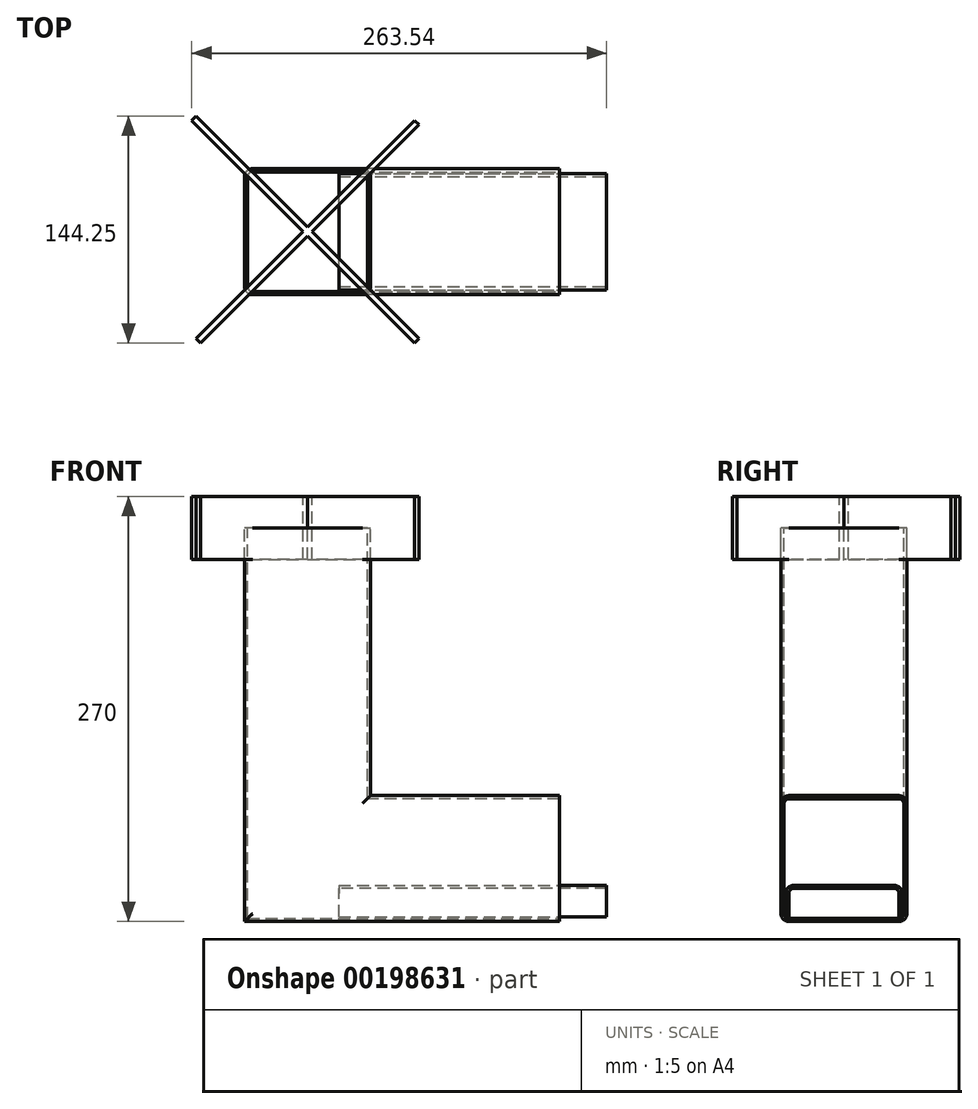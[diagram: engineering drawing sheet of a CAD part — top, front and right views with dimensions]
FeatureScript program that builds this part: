
annotation { "Feature Type Name" : "Feature", "Feature Type Description" : "" }
export const myFeature = defineFeature(function(context is Context, id is Id, definition is map)
    precondition{}
    {
        {
            var Q0;
            Q0=qCreatedBy(makeId("Front.planeOp"),FACE);
            var sketch = newSketch(context, id + "F0", { "sketchPlane" : qUnion([Q0])});
            skLineSegment(sketch, "E0.bottom", {"start": v(0, 0) * mm, "end": v(80, 0) * mm});
            skLineSegment(sketch, "E0.top", {"start": v(0, 250) * mm, "end": v(80, 250) * mm});
            skLineSegment(sketch, "E0.left", {"start": v(0, 0) * mm, "end": v(0, 250) * mm});
            skLineSegment(sketch, "E0.right", {"start": v(80, 0) * mm, "end": v(80, 250) * mm});
            skLineSegment(sketch, "E1", {"start": v(0, 0) * mm, "end": v(200, 0) * mm});
            skLineSegment(sketch, "E2", {"start": v(200, 0) * mm, "end": v(200, 80) * mm});
            skLineSegment(sketch, "E3", {"start": v(200, 80) * mm, "end": v(80, 80) * mm});
            skSolve(sketch);
        }
        {
            var Q0;
            Q0 = qSketchRegion(id + "F0", true);
            extrude(context, id + "F1", {"entities" : qUnion([Q0]), "depth" : 80 * mm});
        }
        {
            var Q0;
            Q0=makeQuery(id+"F1.opExtrude","CAP_EDGE",EDGE,{"disambiguationData":[OSD([sQuery(id+"F0.wireOp",EDGE,"E0.right")])],"isStart":false});
            var Q1;
            Q1=makeQuery(id+"F1.opExtrude","CAP_EDGE",EDGE,{"disambiguationData":[OSD([sQuery(id+"F0.wireOp",EDGE,"E0.right")])],"isStart":true});
            var Q2;
            Q2=makeQuery(id+"F1.opExtrude","CAP_EDGE",EDGE,{"disambiguationData":[OSD([sQuery(id+"F0.wireOp",EDGE,"E0.left")])],"isStart":false});
            var Q3;
            Q3=makeQuery(id+"F1.opExtrude","CAP_EDGE",EDGE,{"disambiguationData":[OSD([sQuery(id+"F0.wireOp",EDGE,"E3")])],"isStart":false});
            var Q4;
            Q4=makeQuery(id+"F1.opExtrude","CAP_EDGE",EDGE,{"disambiguationData":[OSD([sQuery(id+"F0.wireOp",EDGE,"E3")])],"isStart":true});
            var Q5;
            Q5=makeQuery(id+"F1.opExtrude","CAP_EDGE",EDGE,{"disambiguationData":[OSD([sQuery(id+"F0.wireOp",EDGE,"E1")])],"isStart":false});
            var Q6;
            Q6=makeQuery(id+"F1.opExtrude","CAP_EDGE",EDGE,{"disambiguationData":[OSD([sQuery(id+"F0.wireOp",EDGE,"E1")])],"isStart":true});
            var Q7;
            Q7=makeQuery(id+"F1.opExtrude","CAP_EDGE",EDGE,{"disambiguationData":[OSD([sQuery(id+"F0.wireOp",EDGE,"E0.left")])],"isStart":true});
            fillet(context, id + "F2", {"entities" : qUnion([Q0, Q1, Q2, Q3, Q4, Q5, Q6, Q7]), "radius" : 5 * mm, "tangentPropagation" : true, "allowEdgeOverflow" : false});
        }
        {
            var Q0;
            Q0=makeQuery(id+"F1.opExtrude","SWEPT_FACE",FACE,{"disambiguationData":[OSD([sQuery(id+"F0.wireOp",EDGE,"E0.top")])]});
            var Q1;
            Q1=makeQuery(id+"F1.opExtrude","SWEPT_FACE",FACE,{"disambiguationData":[OSD([sQuery(id+"F0.wireOp",EDGE,"E2")])]});
            shell(context, id + "F3", {"entities" : qUnion([Q0, Q1]), "thickness" : 2 * mm});
        }
        {
            var Q0;
            Q0=makeQuery(id+"F1.opExtrude","SWEPT_FACE",FACE,{"disambiguationData":[OSD([sQuery(id+"F0.wireOp",EDGE,"E0.top")])]});
            cPlane(context, id + "F4", {"entities" : qUnion([Q0]), "cplaneType" : CPlaneType.OFFSET, "offset" : 20 * mm, "width" : 150 * mm, "height" : 150 * mm});
        }
        {
            var Q0;
            Q0=qCreatedBy(id+"F4.planeOp",FACE);
            var sketch = newSketch(context, id + "F5", { "sketchPlane" : qUnion([Q0])});
            skLineSegment(sketch, "E4", {"start": v(-33.54, 30.71) * mm, "end": v(107.88, -110.71) * mm});
            skLineSegment(sketch, "E5", {"start": v(110.71, -107.88) * mm, "end": v(107.88, -110.71) * mm});
            skLineSegment(sketch, "E6", {"start": v(110.71, -107.88) * mm, "end": v(-30.71, 33.54) * mm});
            skLineSegment(sketch, "E7", {"start": v(-33.54, 30.71) * mm, "end": v(-30.71, 33.54) * mm});
            skLineSegment(sketch, "E8", {"start": v(-32.12, 32.12) * mm, "end": v(109.3, -109.3) * mm, "construction": true});
            skLineSegment(sketch, "E9", {"start": v(-30.71, -107.88) * mm, "end": v(107.88, 30.71) * mm});
            skLineSegment(sketch, "E10", {"start": v(107.88, 30.71) * mm, "end": v(110.71, 27.88) * mm});
            skLineSegment(sketch, "E11", {"start": v(110.71, 27.88) * mm, "end": v(-27.88, -110.71) * mm});
            skLineSegment(sketch, "E12", {"start": v(-27.88, -110.71) * mm, "end": v(-30.71, -107.88) * mm});
            skLineSegment(sketch, "E13", {"start": v(109.3, 29.3) * mm, "end": v(-29.3, -109.3) * mm, "construction": true});
            skLineSegment(sketch, "E14", {"start": v(-33.54, 30.71) * mm, "end": v(107.88, 30.71) * mm, "construction": true});
            skLineSegment(sketch, "E15", {"start": v(-30.71, 33.54) * mm, "end": v(-30.71, -107.88) * mm, "construction": true});
            skLineSegment(sketch, "E16", {"start": v(110.71, 27.88) * mm, "end": v(110.71, -107.88) * mm, "construction": true});
            skSolve(sketch);
        }
        {
            var Q0;
            {var subQ0=sQuery(id+"F5.wireOp",EDGE,"E7");Q0=makeQuery(id+"F5.imprint","IMPRINT",FACE,{"disambiguationData":[TD([[makeQuery(id+"F5.imprint","IMPRINT",EDGE,{"derivedFrom":subQ0}),-1.0]])]});}
            var Q1;
            {var subQ5=sQuery(id+"F5.wireOp",EDGE,"E10");Q1=makeQuery(id+"F5.imprint","IMPRINT",FACE,{"disambiguationData":[TD([[makeQuery(id+"F5.imprint","IMPRINT",EDGE,{"derivedFrom":subQ5}),-1.0]])]});}
            var Q2;
            {var subQ0=sQuery(id+"F5.wireOp",EDGE,"E9");var subQ1=sQuery(id+"F5.wireOp",EDGE,"E4");var subQ2=makeQuery(id+"F5.imprint","INTERSECT",VERTEX,{"derivedFrom":[subQ1,subQ0]});Q2=makeQuery(id+"F5.imprint","IMPRINT",FACE,{"disambiguationData":[TD([[makeQuery(id+"F5.imprint","IMPRINT",EDGE,{"disambiguationData":[TD([[subQ2,-1.0]])],"derivedFrom":subQ1}),1.0]])]});}
            var Q3;
            {var subQ5=sQuery(id+"F5.wireOp",EDGE,"E12");Q3=makeQuery(id+"F5.imprint","IMPRINT",FACE,{"disambiguationData":[TD([[makeQuery(id+"F5.imprint","IMPRINT",EDGE,{"derivedFrom":subQ5}),-1.0]])]});}
            var Q4;
            {var subQ0=sQuery(id+"F5.wireOp",EDGE,"E5");Q4=makeQuery(id+"F5.imprint","IMPRINT",FACE,{"disambiguationData":[TD([[makeQuery(id+"F5.imprint","IMPRINT",EDGE,{"derivedFrom":subQ0}),-1.0]])]});}
            extrude(context, id + "F6", {"entities" : qUnion([Q0, Q1, Q2, Q3, Q4]), "oppositeDirection" : true, "depth" : 40 * mm});
        }
        {
            var Q0;
            Q0=makeQuery(id+"F1.opExtrude","SWEPT_FACE",FACE,{"disambiguationData":[OSD([sQuery(id+"F0.wireOp",EDGE,"E2")])]});
            var sketch = newSketch(context, id + "F7", { "sketchPlane" : qUnion([Q0])});
            skLineSegment(sketch, "E17", {"start": v(-77, 3) * mm, "end": v(-77, 23) * mm});
            skLineSegment(sketch, "E18", {"start": v(-77, 23) * mm, "end": v(-3, 23) * mm});
            skLineSegment(sketch, "E19", {"start": v(-3, 23) * mm, "end": v(-3, 3) * mm});
            skLineSegment(sketch, "E20", {"start": v(-3, 3) * mm, "end": v(-77, 3) * mm});
            skSolve(sketch);
        }
        {
            var Q0;
            Q0=makeQuery(id+"F7.imprint","IMPRINT",FACE,{"disambiguationData":[TD([[makeQuery(id+"F7.imprint","IMPRINT",EDGE,{"derivedFrom":sQuery(id+"F7.wireOp",EDGE,"E17")}),-1.0]])]});
            extrude(context, id + "F8", {"entities" : qUnion([Q0]), "oppositeDirection" : true, "depth" : 140 * mm, "hasSecondDirection" : true, "secondDirectionOppositeDirection" : false, "secondDirectionDepth" : 30 * mm});
        }
        {
            var Q0;
            Q0=makeQuery(id+"F8.opExtrude","SWEPT_EDGE",EDGE,{"disambiguationData":[OSD([sQuery(id+"F7.wireOp",EDGE,"E17"),sQuery(id+"F7.wireOp",EDGE,"E18")])]});
            var Q1;
            Q1=makeQuery(id+"F8.opExtrude","SWEPT_EDGE",EDGE,{"disambiguationData":[OSD([sQuery(id+"F7.wireOp",EDGE,"E18"),sQuery(id+"F7.wireOp",EDGE,"E19")])]});
            fillet(context, id + "F9", {"entities" : qUnion([Q0, Q1]), "radius" : 5 * mm, "tangentPropagation" : true, "allowEdgeOverflow" : false});
        }
        {
            var Q0;
            Q0=makeQuery(id+"F8.opExtrude","SWEPT_FACE",FACE,{"disambiguationData":[OSD([sQuery(id+"F7.wireOp",EDGE,"E20")])]});
            var Q1;
            Q1=makeQuery(id+"F8.opExtrude","CAP_FACE",FACE,{"disambiguationData":[OSD([sQuery(id+"F7.wireOp",EDGE,"E17"),sQuery(id+"F7.wireOp",EDGE,"E18"),sQuery(id+"F7.wireOp",EDGE,"E19"),sQuery(id+"F7.wireOp",EDGE,"E20")])],"isStart":false});
            var Q2;
            Q2=makeQuery(id+"F8.opExtrude","CAP_FACE",FACE,{"disambiguationData":[OSD([sQuery(id+"F7.wireOp",EDGE,"E17"),sQuery(id+"F7.wireOp",EDGE,"E18"),sQuery(id+"F7.wireOp",EDGE,"E19"),sQuery(id+"F7.wireOp",EDGE,"E20")])],"isStart":true});
            shell(context, id + "F10", {"entities" : qUnion([Q0, Q1, Q2]), "thickness" : 2 * mm});
        }
    });
